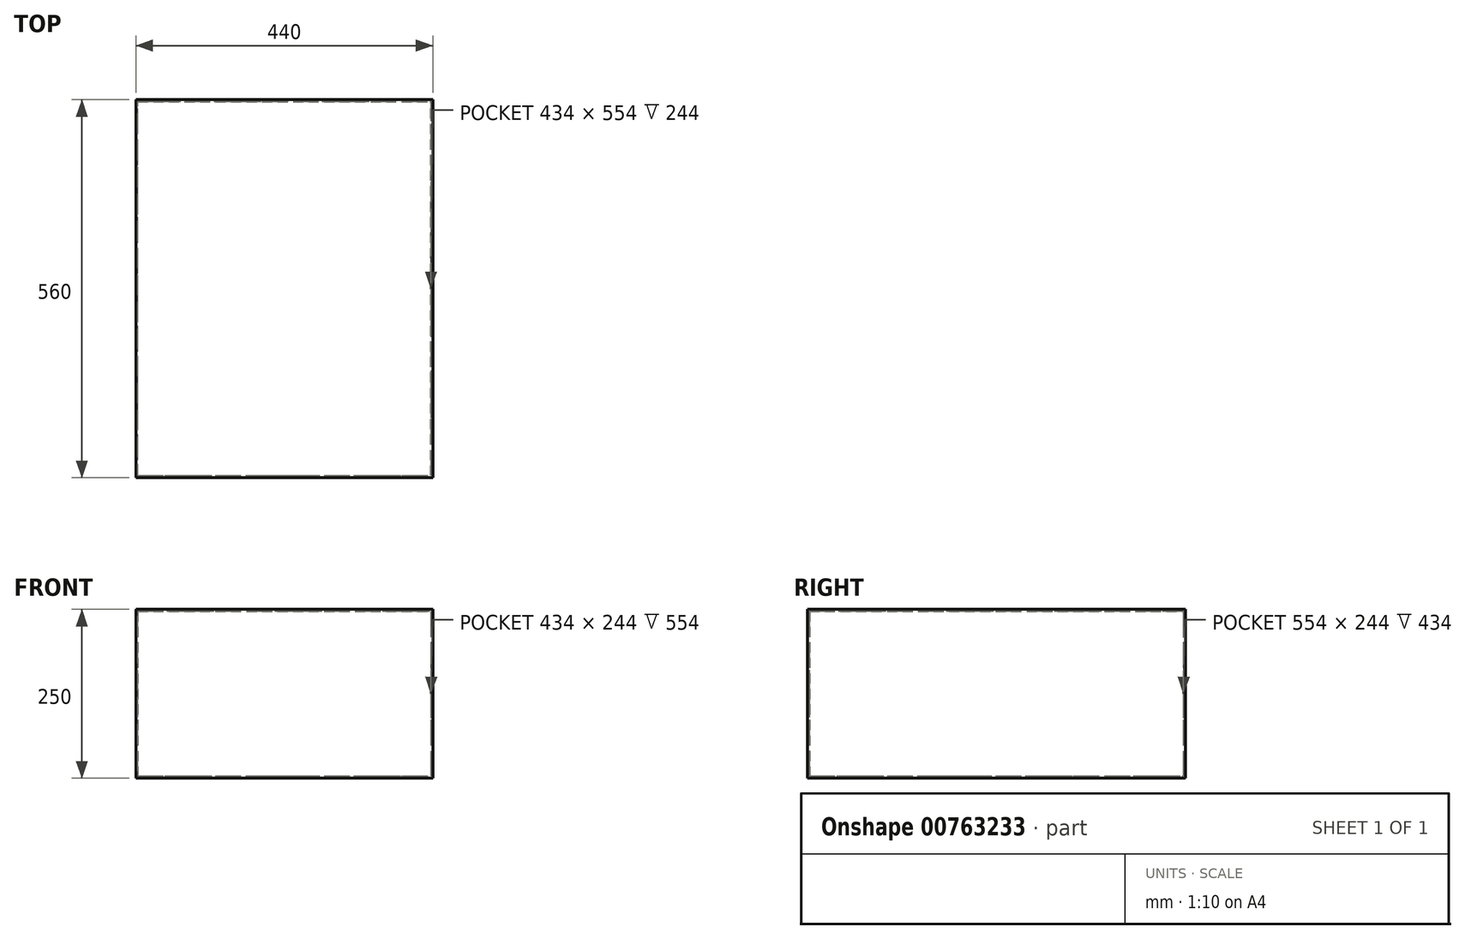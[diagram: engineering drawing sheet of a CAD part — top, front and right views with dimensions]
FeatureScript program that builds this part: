
annotation { "Feature Type Name" : "Feature", "Feature Type Description" : "" }
export const myFeature = defineFeature(function(context is Context, id is Id, definition is map)
    precondition{}
    {
        {
            var Q0;
            Q0=qCreatedBy(makeId("Front.planeOp"),FACE);
            var sketch = newSketch(context, id + "F0", { "sketchPlane" : qUnion([Q0])});
            skLineSegment(sketch, "E0.bottom", {"start": v(-220, 0) * mm, "end": v(220, 0) * mm});
            skLineSegment(sketch, "E0.top", {"start": v(-220, 250) * mm, "end": v(220, 250) * mm});
            skLineSegment(sketch, "E0.left", {"start": v(-220, 0) * mm, "end": v(-220, 250) * mm});
            skLineSegment(sketch, "E0.right", {"start": v(220, 0) * mm, "end": v(220, 250) * mm});
            skLineSegment(sketch, "E1.bottom", {"start": v(-217, 247) * mm, "end": v(217, 247) * mm});
            skLineSegment(sketch, "E1.top", {"start": v(-217, 3) * mm, "end": v(217, 3) * mm});
            skLineSegment(sketch, "E1.left", {"start": v(-217, 247) * mm, "end": v(-217, 3) * mm});
            skLineSegment(sketch, "E1.right", {"start": v(217, 247) * mm, "end": v(217, 3) * mm});
            skSolve(sketch);
        }
        {
            var Q0;
            Q0=makeQuery(id+"F0.imprint","IMPRINT",FACE,{"disambiguationData":[TD([[makeQuery(id+"F0.imprint","IMPRINT",EDGE,{"derivedFrom":sQuery(id+"F0.wireOp",EDGE,"E0.bottom")}),1.0]])]});
            extrude(context, id + "F1", {"entities" : qUnion([Q0]), "endBound" : BoundingType.SYMMETRIC, "depth" : 554 * mm, "offsetDistance" : 25.4 * mm});
        }
        {
            var Q0;
            Q0=makeQuery(id+"F1.opExtrude","CAP_FACE",FACE,{"disambiguationData":[OSD([sQuery(id+"F0.wireOp",EDGE,"E0.bottom"),sQuery(id+"F0.wireOp",EDGE,"E0.top"),sQuery(id+"F0.wireOp",EDGE,"E0.left"),sQuery(id+"F0.wireOp",EDGE,"E0.right"),sQuery(id+"F0.wireOp",EDGE,"E1.bottom"),sQuery(id+"F0.wireOp",EDGE,"E1.top"),sQuery(id+"F0.wireOp",EDGE,"E1.left"),sQuery(id+"F0.wireOp",EDGE,"E1.right")])],"isStart":false});
            var sketch = newSketch(context, id + "F2", { "sketchPlane" : qUnion([Q0])});
            skLineSegment(sketch, "E2.bottom", {"start": v(-220, 250) * mm, "end": v(220, 250) * mm});
            skLineSegment(sketch, "E2.top", {"start": v(-220, 0) * mm, "end": v(220, 0) * mm});
            skLineSegment(sketch, "E2.left", {"start": v(-220, 250) * mm, "end": v(-220, 0) * mm});
            skLineSegment(sketch, "E2.right", {"start": v(220, 250) * mm, "end": v(220, 0) * mm});
            skSolve(sketch);
        }
        {
            var Q0;
            Q0 = qSketchRegion(id + "F2", true);
            extrude(context, id + "F3", {"entities" : qUnion([Q0]), "operationType" : NewBodyOperationType.ADD, "depth" : 3 * mm, "offsetDistance" : 25.4 * mm});
        }
        {
            var Q0;
            Q0=makeQuery(id+"F1.opExtrude","CAP_FACE",FACE,{"disambiguationData":[OSD([sQuery(id+"F0.wireOp",EDGE,"E0.bottom"),sQuery(id+"F0.wireOp",EDGE,"E0.top"),sQuery(id+"F0.wireOp",EDGE,"E0.left"),sQuery(id+"F0.wireOp",EDGE,"E0.right"),sQuery(id+"F0.wireOp",EDGE,"E1.bottom"),sQuery(id+"F0.wireOp",EDGE,"E1.top"),sQuery(id+"F0.wireOp",EDGE,"E1.left"),sQuery(id+"F0.wireOp",EDGE,"E1.right")])],"isStart":true});
            var sketch = newSketch(context, id + "F4", { "sketchPlane" : qUnion([Q0])});
            skLineSegment(sketch, "E3.bottom", {"start": v(-220, 250) * mm, "end": v(220, 250) * mm});
            skLineSegment(sketch, "E3.top", {"start": v(-220, 0) * mm, "end": v(220, 0) * mm});
            skLineSegment(sketch, "E3.left", {"start": v(-220, 250) * mm, "end": v(-220, 0) * mm});
            skLineSegment(sketch, "E3.right", {"start": v(220, 250) * mm, "end": v(220, 0) * mm});
            skSolve(sketch);
        }
        {
            var Q0;
            Q0 = qSketchRegion(id + "F4", true);
            extrude(context, id + "F5", {"entities" : qUnion([Q0]), "operationType" : NewBodyOperationType.ADD, "depth" : 3 * mm, "offsetDistance" : 25.4 * mm});
        }
    });
